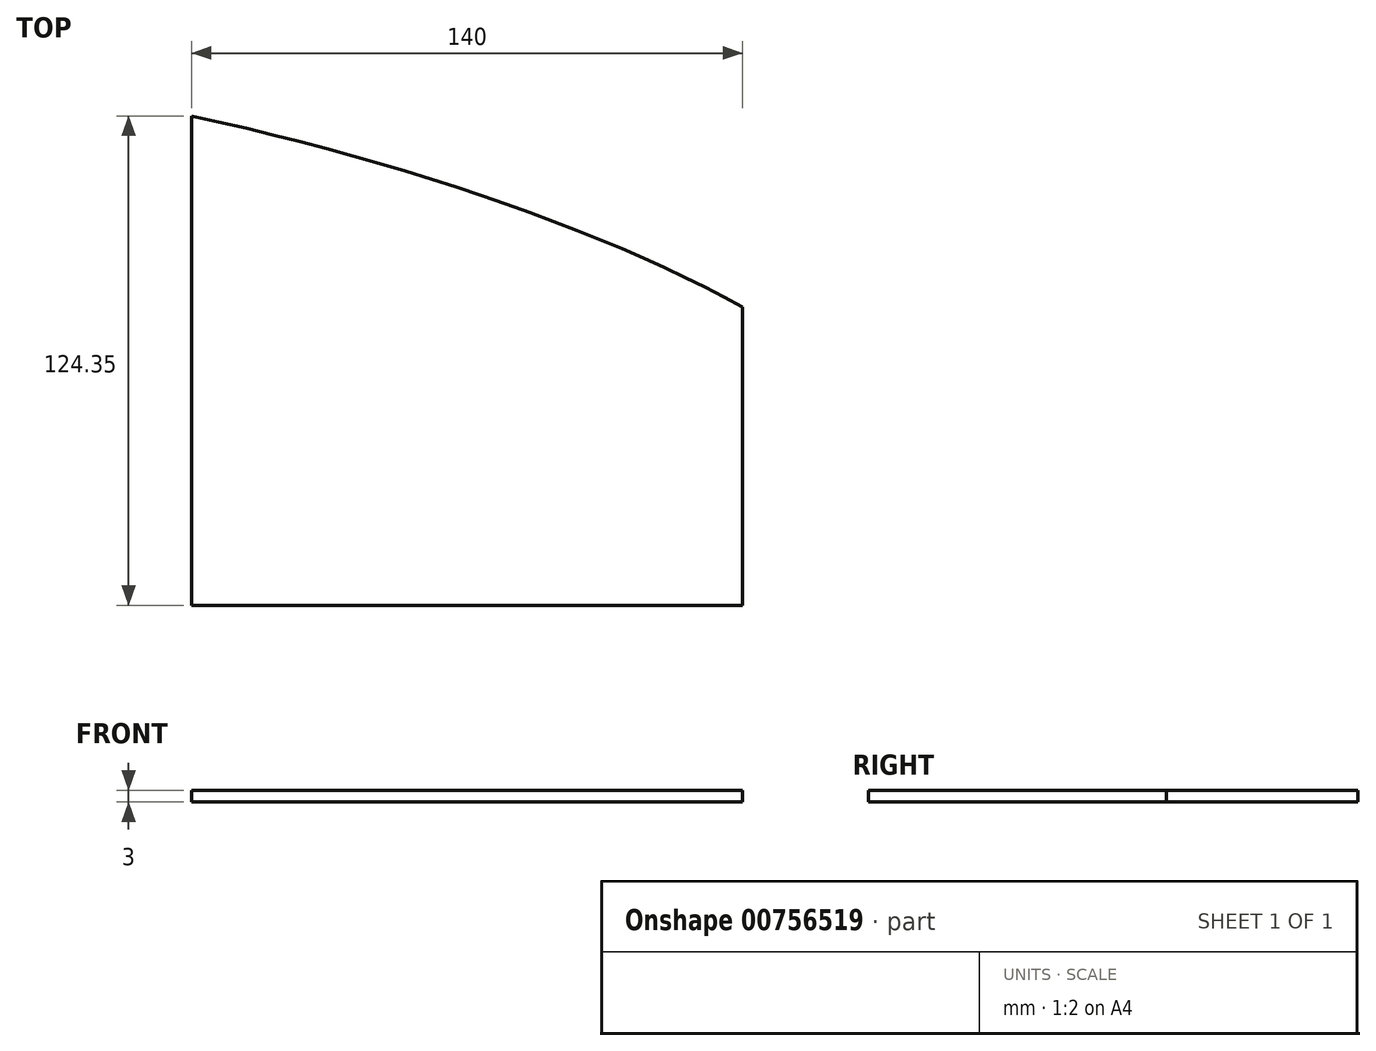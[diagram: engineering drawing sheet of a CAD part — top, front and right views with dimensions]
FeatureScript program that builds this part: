
annotation { "Feature Type Name" : "Feature", "Feature Type Description" : "" }
export const myFeature = defineFeature(function(context is Context, id is Id, definition is map)
    precondition{}
    {
        {
            var Q0;
            Q0=qCreatedBy(makeId("Top.planeOp"),FACE);
            var sketch = newSketch(context, id + "F0", { "sketchPlane" : qUnion([Q0])});
            skLineSegment(sketch, "E0.right", {"start": v(-155, -140) * mm, "end": v(-155, 140) * mm});
            skPoint(sketch, "E0.middle", {"position": v(0, 0) * mm});
            skLineSegment(sketch, "E1", {"start": v(155, 0) * mm, "end": v(155, 50) * mm});
            skLineSegment(sketch, "E2", {"start": v(155, 0) * mm, "end": v(155, -50) * mm});
            skLineSegment(sketch, "E3", {"start": v(155, 0) * mm, "end": v(175, 0) * mm});
            skLineSegment(sketch, "E4", {"start": v(-155, 140) * mm, "end": v(-155, -140) * mm});
            skFitSpline(sketch, "E5", {"points": [v(-155, 140) * mm, v(155, 50) * mm, v(175, 0) * mm], "startDerivative": vector(449.36, 4.91) * mm, "endDerivative": vector(26.44, -99.47) * mm});
            skLineSegment(sketch, "E6", {"start": v(-155, 0) * mm, "end": v(155, 0) * mm});
            skSolve(sketch);
        }
        {
            var Q0;
            Q0=qSketchRegion(id+"F0",true);
            var Q1;
            {var subQ0=sQuery(id+"F0.wireOp",EDGE,"E1");Q1=makeQuery(id+"F0.imprint","IMPRINT",FACE,{"disambiguationData":[TD([[makeQuery(id+"F0.imprint","IMPRINT",EDGE,{"derivedFrom":subQ0}),1.0]])]});}
            extrude(context, id + "F1", {"entities" : qUnion([Q0, Q1]), "depth" : 3 * mm, "offsetDistance" : 25 * mm});
        }
        {
            var Q0;
            Q0=qCreatedBy(makeId("Top.planeOp"),FACE);
            var sketch = newSketch(context, id + "F2", { "sketchPlane" : qUnion([Q0])});
            skLineSegment(sketch, "E7.bottom", {"start": v(450, -150) * mm, "end": v(-450, -150) * mm});
            skLineSegment(sketch, "E7.top", {"start": v(450, 150) * mm, "end": v(-450, 150) * mm});
            skLineSegment(sketch, "E7.left", {"start": v(450, -150) * mm, "end": v(450, 150) * mm});
            skLineSegment(sketch, "E7.right", {"start": v(-450, -150) * mm, "end": v(-450, 150) * mm});
            skPoint(sketch, "E7.middle", {"position": v(0, 0) * mm});
            skLineSegment(sketch, "E8.bottom", {"start": v(70, -147.5) * mm, "end": v(-70, -147.5) * mm});
            skLineSegment(sketch, "E8.top", {"start": v(70, 147.5) * mm, "end": v(-70, 147.5) * mm});
            skLineSegment(sketch, "E8.left", {"start": v(70, -147.5) * mm, "end": v(70, 147.5) * mm});
            skLineSegment(sketch, "E8.right", {"start": v(-70, -147.5) * mm, "end": v(-70, 147.5) * mm});
            skSolve(sketch);
        }
        {
            var Q0;
            Q0=qSketchRegion(id+"F2",true);
            extrude(context, id + "F3", {"entities" : qUnion([Q0]), "depth" : 25 * mm, "offsetDistance" : 25 * mm});
        }
        {
            var Q0;
            Q0=makeQuery(id+"F3.opExtrude","SWEPT_BODY",BODY,{"disambiguationData":[OSD([sQuery(id+"F2.wireOp",EDGE,"E7.bottom"),sQuery(id+"F2.wireOp",EDGE,"E7.top"),sQuery(id+"F2.wireOp",EDGE,"E7.left"),sQuery(id+"F2.wireOp",EDGE,"E7.right"),sQuery(id+"F2.wireOp",EDGE,"E8.bottom"),sQuery(id+"F2.wireOp",EDGE,"E8.top"),sQuery(id+"F2.wireOp",EDGE,"E8.left"),sQuery(id+"F2.wireOp",EDGE,"E8.right")])]});
            transform(context, id + "F4", {"entities" : qUnion([Q0]), "transformType" : TransformType.TRANSLATION_3D, "dx" : 50 * mm, "dy" : 0 * mm, "dz" : 0 * mm, "makeCopy" : false});
        }
        {
            var Q0;
            Q0=makeQuery(id+"F3.opExtrude","SWEPT_BODY",BODY,{"disambiguationData":[OSD([sQuery(id+"F2.wireOp",EDGE,"E7.bottom"),sQuery(id+"F2.wireOp",EDGE,"E7.top"),sQuery(id+"F2.wireOp",EDGE,"E7.left"),sQuery(id+"F2.wireOp",EDGE,"E7.right"),sQuery(id+"F2.wireOp",EDGE,"E8.bottom"),sQuery(id+"F2.wireOp",EDGE,"E8.top"),sQuery(id+"F2.wireOp",EDGE,"E8.left"),sQuery(id+"F2.wireOp",EDGE,"E8.right")])]});
            var Q1;
            Q1=makeQuery(id+"F1.opExtrude","SWEPT_BODY",BODY,{"disambiguationData":[OSD([sQuery(id+"F0.wireOp",EDGE,"E3"),sQuery(id+"F0.wireOp",EDGE,"E4"),sQuery(id+"F0.wireOp",EDGE,"E5"),sQuery(id+"F0.wireOp",EDGE,"E6")])]});
            booleanBodies(context, id + "F5", {"operationType" : BooleanOperationType.SUBTRACTION, "tools" : qUnion([Q0]), "targets" : qUnion([Q1])});
        }
    });
